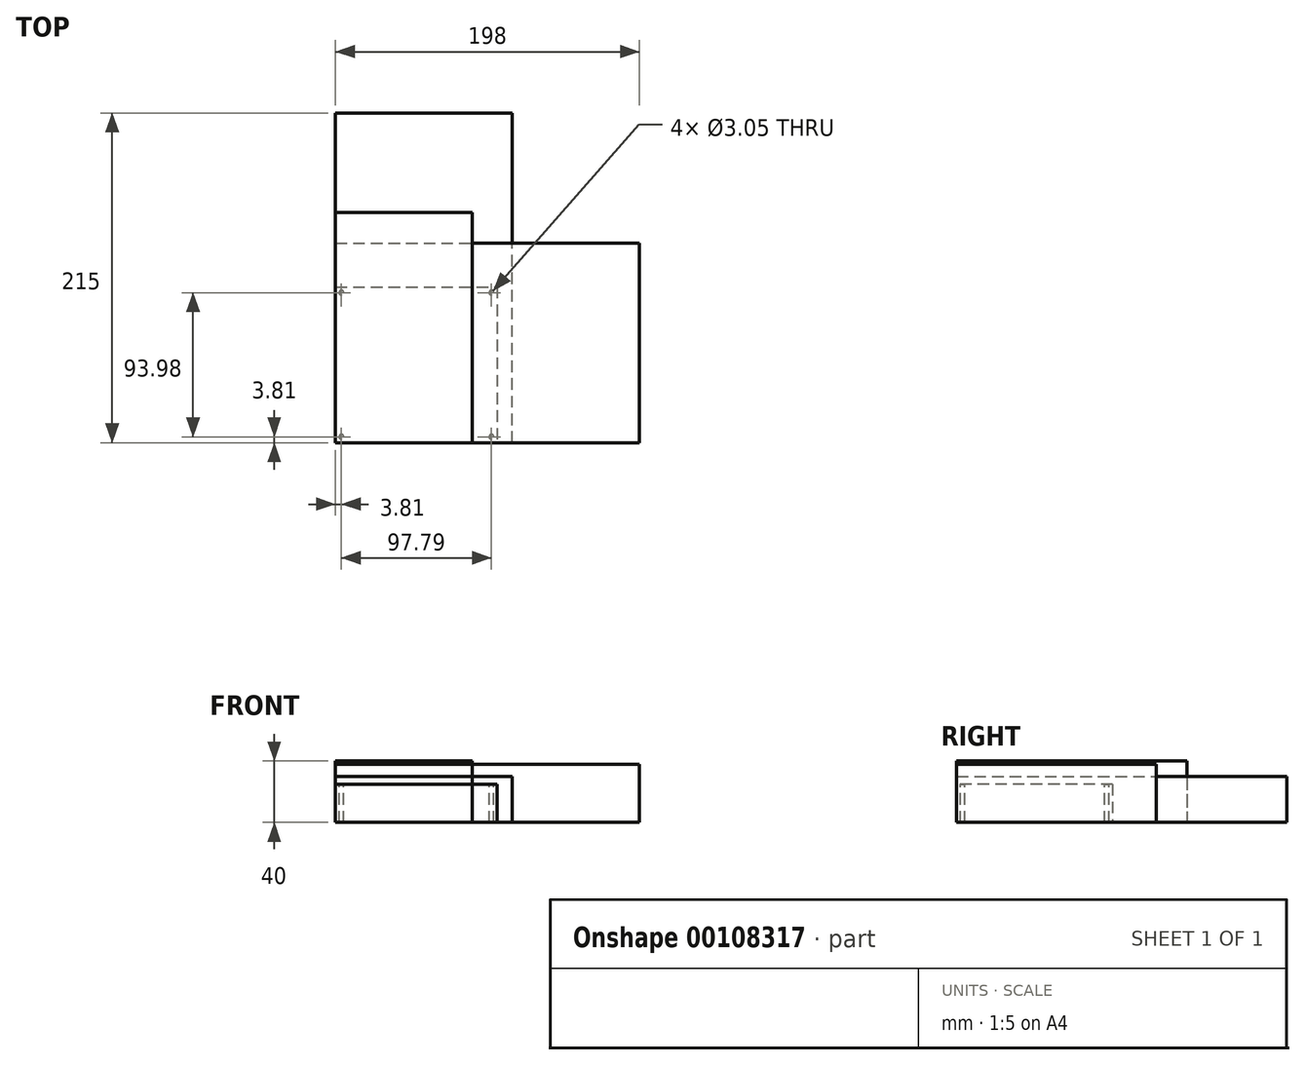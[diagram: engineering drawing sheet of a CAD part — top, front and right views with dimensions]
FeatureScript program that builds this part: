
annotation { "Feature Type Name" : "Feature", "Feature Type Description" : "" }
export const myFeature = defineFeature(function(context is Context, id is Id, definition is map)
    precondition{}
    {
        {
            var Q0;
            Q0=qCreatedBy(makeId("Top.planeOp"),FACE);
            var sketch = newSketch(context, id + "F0", { "sketchPlane" : qUnion([Q0])});
            skLineSegment(sketch, "E0.bottom", {"start": v(0, 101.6) * mm, "end": v(105.4, 101.6) * mm});
            skLineSegment(sketch, "E0.top", {"start": v(0, 0) * mm, "end": v(105.4, 0) * mm});
            skLineSegment(sketch, "E0.left", {"start": v(0, 101.6) * mm, "end": v(0, 0) * mm});
            skLineSegment(sketch, "E0.right", {"start": v(105.4, 101.6) * mm, "end": v(105.4, 0) * mm});
            skSolve(sketch);
        }
        {
            var Q0;
            Q0=makeQuery(id+"F0.imprint","IMPRINT",FACE,{"disambiguationData":[TD([[makeQuery(id+"F0.imprint","IMPRINT",EDGE,{"derivedFrom":sQuery(id+"F0.wireOp",EDGE,"E0.bottom")}),-1.0]])]});
            extrude(context, id + "F1", {"entities" : qUnion([Q0]), "depth" : 25 * mm});
        }
        {
            var Q0;
            Q0=makeQuery(id+"F1.opExtrude","CAP_FACE",FACE,{"disambiguationData":[OSD([sQuery(id+"F0.wireOp",EDGE,"E0.bottom"),sQuery(id+"F0.wireOp",EDGE,"E0.top"),sQuery(id+"F0.wireOp",EDGE,"E0.left"),sQuery(id+"F0.wireOp",EDGE,"E0.right")])],"isStart":false});
            var sketch = newSketch(context, id + "F2", { "sketchPlane" : qUnion([Q0])});
            skLineSegment(sketch, "E1.bottom", {"start": v(3.8, 97.8) * mm, "end": v(101.6, 97.8) * mm});
            skLineSegment(sketch, "E1.top", {"start": v(3.8, 3.81) * mm, "end": v(101.6, 3.81) * mm});
            skLineSegment(sketch, "E1.left", {"start": v(3.8, 97.8) * mm, "end": v(3.8, 3.81) * mm});
            skLineSegment(sketch, "E1.right", {"start": v(101.6, 97.8) * mm, "end": v(101.6, 3.81) * mm});
            skSolve(sketch);
        }
        {
            var Q0;
            Q0=sQuery(id+"F2.wireOp",VERTEX,"E1.left.start");
            var Q1;
            Q1=makeQuery(id+"F1.opExtrude","SWEPT_BODY",BODY,{"disambiguationData":[OSD([sQuery(id+"F0.wireOp",EDGE,"E0.bottom"),sQuery(id+"F0.wireOp",EDGE,"E0.top"),sQuery(id+"F0.wireOp",EDGE,"E0.left"),sQuery(id+"F0.wireOp",EDGE,"E0.right")])]});
            hole(context, id + "F3", {"style" : HoleStyle.SIMPLE, "endStyle" : HoleEndStyle.THROUGH, "holeDiameter" : (.12 * 25.4) * mm, "locations" : qUnion([Q0]), "scope" : qUnion([Q1]), "isTappedThrough" : true});
        }
        {
            var Q0;
            Q0=sQuery(id+"F2.wireOp",VERTEX,"E1.right.start");
            var Q1;
            Q1=makeQuery(id+"F1.opExtrude","SWEPT_BODY",BODY,{"disambiguationData":[OSD([sQuery(id+"F0.wireOp",EDGE,"E0.bottom"),sQuery(id+"F0.wireOp",EDGE,"E0.top"),sQuery(id+"F0.wireOp",EDGE,"E0.left"),sQuery(id+"F0.wireOp",EDGE,"E0.right")])]});
            hole(context, id + "F4", {"style" : HoleStyle.SIMPLE, "endStyle" : HoleEndStyle.THROUGH, "holeDiameter" : (.12 * 25.4) * mm, "locations" : qUnion([Q0]), "scope" : qUnion([Q1]), "isTappedThrough" : true});
        }
        {
            var Q0;
            Q0=sQuery(id+"F2.wireOp",VERTEX,"E1.left.end");
            var Q1;
            Q1=makeQuery(id+"F1.opExtrude","SWEPT_BODY",BODY,{"disambiguationData":[OSD([sQuery(id+"F0.wireOp",EDGE,"E0.bottom"),sQuery(id+"F0.wireOp",EDGE,"E0.top"),sQuery(id+"F0.wireOp",EDGE,"E0.left"),sQuery(id+"F0.wireOp",EDGE,"E0.right")])]});
            hole(context, id + "F5", {"style" : HoleStyle.SIMPLE, "endStyle" : HoleEndStyle.THROUGH, "holeDiameter" : (.12 * 25.4) * mm, "locations" : qUnion([Q0]), "scope" : qUnion([Q1]), "isTappedThrough" : true});
        }
        {
            var Q0;
            Q0=sQuery(id+"F2.wireOp",VERTEX,"E1.top.end");
            var Q1;
            Q1=makeQuery(id+"F1.opExtrude","SWEPT_BODY",BODY,{"disambiguationData":[OSD([sQuery(id+"F0.wireOp",EDGE,"E0.bottom"),sQuery(id+"F0.wireOp",EDGE,"E0.top"),sQuery(id+"F0.wireOp",EDGE,"E0.left"),sQuery(id+"F0.wireOp",EDGE,"E0.right")])]});
            hole(context, id + "F6", {"style" : HoleStyle.SIMPLE, "endStyle" : HoleEndStyle.THROUGH, "holeDiameter" : (.12 * 25.4) * mm, "locations" : qUnion([Q0]), "scope" : qUnion([Q1]), "isTappedThrough" : true});
        }
        {
            var Q0;
            Q0=qCreatedBy(makeId("Top.planeOp"),FACE);
            var sketch = newSketch(context, id + "F7", { "sketchPlane" : qUnion([Q0])});
            skLineSegment(sketch, "E2.bottom", {"start": v(0, 0) * mm, "end": v(115, 0) * mm});
            skLineSegment(sketch, "E2.top", {"start": v(0, 215) * mm, "end": v(115, 215) * mm});
            skLineSegment(sketch, "E2.left", {"start": v(0, 0) * mm, "end": v(0, 215) * mm});
            skLineSegment(sketch, "E2.right", {"start": v(115, 0) * mm, "end": v(115, 215) * mm});
            skSolve(sketch);
        }
        {
            var Q0;
            Q0=makeQuery(id+"F7.imprint","IMPRINT",FACE,{"disambiguationData":[TD([[makeQuery(id+"F7.imprint","IMPRINT",EDGE,{"derivedFrom":sQuery(id+"F7.wireOp",EDGE,"E2.bottom")}),1.0]])]});
            extrude(context, id + "F8", {"entities" : qUnion([Q0]), "depth" : 30 * mm});
        }
        {
            var Q0;
            Q0=qCreatedBy(makeId("Top.planeOp"),FACE);
            var sketch = newSketch(context, id + "F9", { "sketchPlane" : qUnion([Q0])});
            skLineSegment(sketch, "E3.bottom", {"start": v(0, 0) * mm, "end": v(198, 0) * mm});
            skLineSegment(sketch, "E3.top", {"start": v(0, 130) * mm, "end": v(198, 130) * mm});
            skLineSegment(sketch, "E3.left", {"start": v(0, 0) * mm, "end": v(0, 130) * mm});
            skLineSegment(sketch, "E3.right", {"start": v(198, 0) * mm, "end": v(198, 130) * mm});
            skSolve(sketch);
        }
        {
            var Q0;
            Q0=qSketchRegion(id+"F9",true);
            var Q1;
            Q1=makeQuery(id+"F9.imprint","IMPRINT",FACE,{"disambiguationData":[TD([[makeQuery(id+"F9.imprint","IMPRINT",EDGE,{"derivedFrom":sQuery(id+"F9.wireOp",EDGE,"E3.bottom")}),1.0]])]});
            extrude(context, id + "F10", {"entities" : qUnion([Q0, Q1]), "depth" : 38 * mm});
        }
        {
            var Q0;
            Q0=qCreatedBy(makeId("Top.planeOp"),FACE);
            var sketch = newSketch(context, id + "F11", { "sketchPlane" : qUnion([Q0])});
            skLineSegment(sketch, "E4.bottom", {"start": v(0, 0) * mm, "end": v(89, 0) * mm});
            skLineSegment(sketch, "E4.top", {"start": v(0, 150) * mm, "end": v(89, 150) * mm});
            skLineSegment(sketch, "E4.left", {"start": v(0, 0) * mm, "end": v(0, 150) * mm});
            skLineSegment(sketch, "E4.right", {"start": v(89, 0) * mm, "end": v(89, 150) * mm});
            skSolve(sketch);
        }
        {
            var Q0;
            Q0=qSketchRegion(id+"F11",true);
            var Q1;
            Q1=makeQuery(id+"F11.imprint","IMPRINT",FACE,{"disambiguationData":[TD([[makeQuery(id+"F11.imprint","IMPRINT",EDGE,{"derivedFrom":sQuery(id+"F11.wireOp",EDGE,"E4.bottom")}),1.0]])]});
            extrude(context, id + "F12", {"entities" : qUnion([Q0, Q1]), "depth" : 40 * mm});
        }
    });
